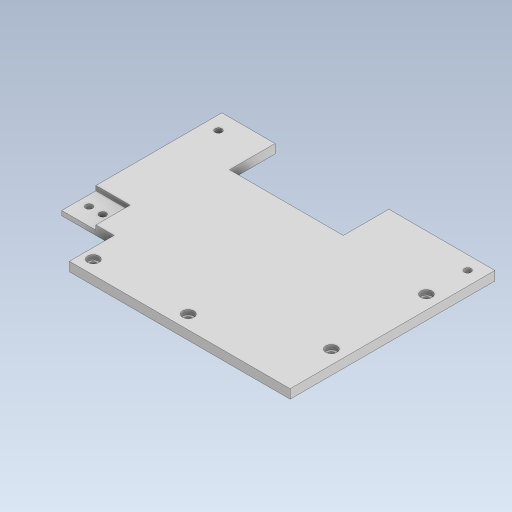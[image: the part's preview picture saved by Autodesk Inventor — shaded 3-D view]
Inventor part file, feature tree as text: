
AUTODESK INVENTOR PART (.ipt)
format: ipt  version: 2023.5 (Build 275446000, 446)  size: 337,920 bytes
history: native  units: in
note: dims shown in document units (in); Inventor stores cm internally (conversion verified against a paired STEP export)
features: extrude x2, sketch x1
ambient origin geometry x8: Origin, YZ Plane, XZ Plane, XY Plane, X Axis, Y Axis, Z Axis, Center Point
bodies: Solid1 (feature_tree)
feature tree (3):
  sketch  "Sketch1"  dims[d28=0.1575in d29=0.0in d30=0.0787in d31=0.0in d32=0.4724in d33=0.2953in d34=0.2953in d35=0.4724in d36=0.0in d37=0.0in d39=0.315in]
  extrude  "Extrusion1"  Depth=0.0787in TaperAngle=0.0deg
  extrude  "Extrusion2"  Depth=0.315in
